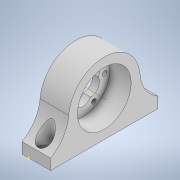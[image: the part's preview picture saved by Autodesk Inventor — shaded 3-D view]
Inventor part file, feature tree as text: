
AUTODESK INVENTOR PART (.ipt)
format: ipt  version: 2020 (Build 240168000, 168)  size: 220,672 bytes
history: native  units: in
note: dims shown in document units (in); Inventor stores cm internally (conversion verified against a paired STEP export)
features: sketch x8, extrude x6, fillet x2, hole x1, other x1, pattern_circular x1
ambient origin geometry x8: Origin, YZ Plane, XZ Plane, XY Plane, X Axis, Y Axis, Z Axis, Center Point
bodies: Solid1 (feature_tree)
feature tree (19):
  extrude  "Extrusion1"  Depth=3.0in
  extrude  "Extrusion2"  Depth=0.5in
  extrude  "Extrusion3"  Depth=1.0in
  fillet  "Fillet1"  Radius=1.7in
  sketch  "Sketch6"  dims[d10=1.5in d11=0.6in d12=0.0in]
  fillet  "Fillet2"  Radius=1.0in
  hole  "Hole1"  [1 undecoded]
  extrude  "Extrusion5"  Depth=0.25in
  extrude  "Extrusion8"  Depth=1.0in
  extrude  "Extrusion9"  Depth=1.0in
  sketch  "Sketch13"  dims[d31=0.4in d32=0.6in d33=0.0in d65=0.25in d66=1.0in d67=0.0in d74=1.0in d75=0.0in d76=2.3622in d77=360.0deg d79=0.61in d80=120.0deg d81=0.61in d82=60.0deg d83=0.13in d84=0.13in]
  other  "Work Axis3"
  pattern_circular  "Circular Pattern3"  [2 undecoded]
  sketch  "Sketch1"  dims[d0=0.8in d1=3.0in]
  sketch  "Sketch2"  dims[d2=0.3in d3=0.0in d4=0.5in]
  sketch  "Sketch3"  dims[d5=0.8in d6=2.0in d7=1.7in d8=0.0in d9=1.0in]
  sketch  "Sketch7"  dims[d19=1.0in d20=0.25in]
  sketch  "Sketch10"  dims[d21=0.25in d22=1.0in]
  sketch  "Sketch12"  dims[d23=0.2in d24=0.75in d25=0.4in d26=0.15in d27=0.5635in d28=1.0in d29=0.8108in d30=0.4in]
note: 3 required parameter values undecoded (feature->parameter linkage not recoverable at this tier; creation-order binding heuristic only, values carry confidence <= 0.55)
